# Revit family: Partition_Corflex_5500_Series_Inside_Pocket
name_source: partatom
category: Specialty Equipment
units: mm (PartAtom-declared; Revit-internal decimal feet)

## family parameters
Always vertical = Yes
Cut with Voids When Loaded = No
Enable Cutting in Views = No
Maintain Annotation Orientation = No
OmniClass Number = 23.25.40.17.11
OmniClass Title = Horizontally Sliding Partitions
Part Type = Normal
Room Calculation Point = No
Round Connector Dimension = Use Diameter
Shared = No
Work Plane-Based = No

## types (3) — shared parameters
Assembly Code = C1010300
CAD Details = https://www.arcat.com
CSI MasterFormat = 10 22 39
CSI MasterFormat 2004 = 10 22 26
Closure Type Lead = Bulb Seal
Closure Type Trail = Lever
Closure Width Lead Standard = 38 mm
Closure Width Trail = 152 mm
Default Elevation = 0 mm
Description = Operable Partition
Enter Pocket Door Type = 3
Finish Material Metal = Corflex - Trim - Beige
Finish Material Panel = Corflex - Vinyl - Blizzard
Finish Material Pocket Door = Corflex - Vinyl - Blizzard
Finish Material Track = Corflex - Track - Clear anodized
Keynote = 10 22 26
Manufacturer = Corflex, Inc.
Manufacturer Telephone = 1 877 410-2422 or (1) 450 444-2441
Model = 5500
Panel Width Max = 1,219 mm
Panel Width Min = 533 mm
Pocket Door Type = 3
Product Page URL = https://www.arcat.com
Specification = https://www.arcat.com
Track Height = 88.9 mm
Track Width = 127 mm
Track Width Above = 88.9 mm
URL = http://www.corflex.ca

## per-type parameters (varying)
| type | Pocket Doors | Pocket Walls |
| Without Pocket | No | No |
| Inside Pocket | No | Yes |
| Inside Pocket with Door | Yes | Yes |

## geometry (parser evidence)
native form markers: Blend x2, Sweep x7
no freeform markers — native parametric forms only
